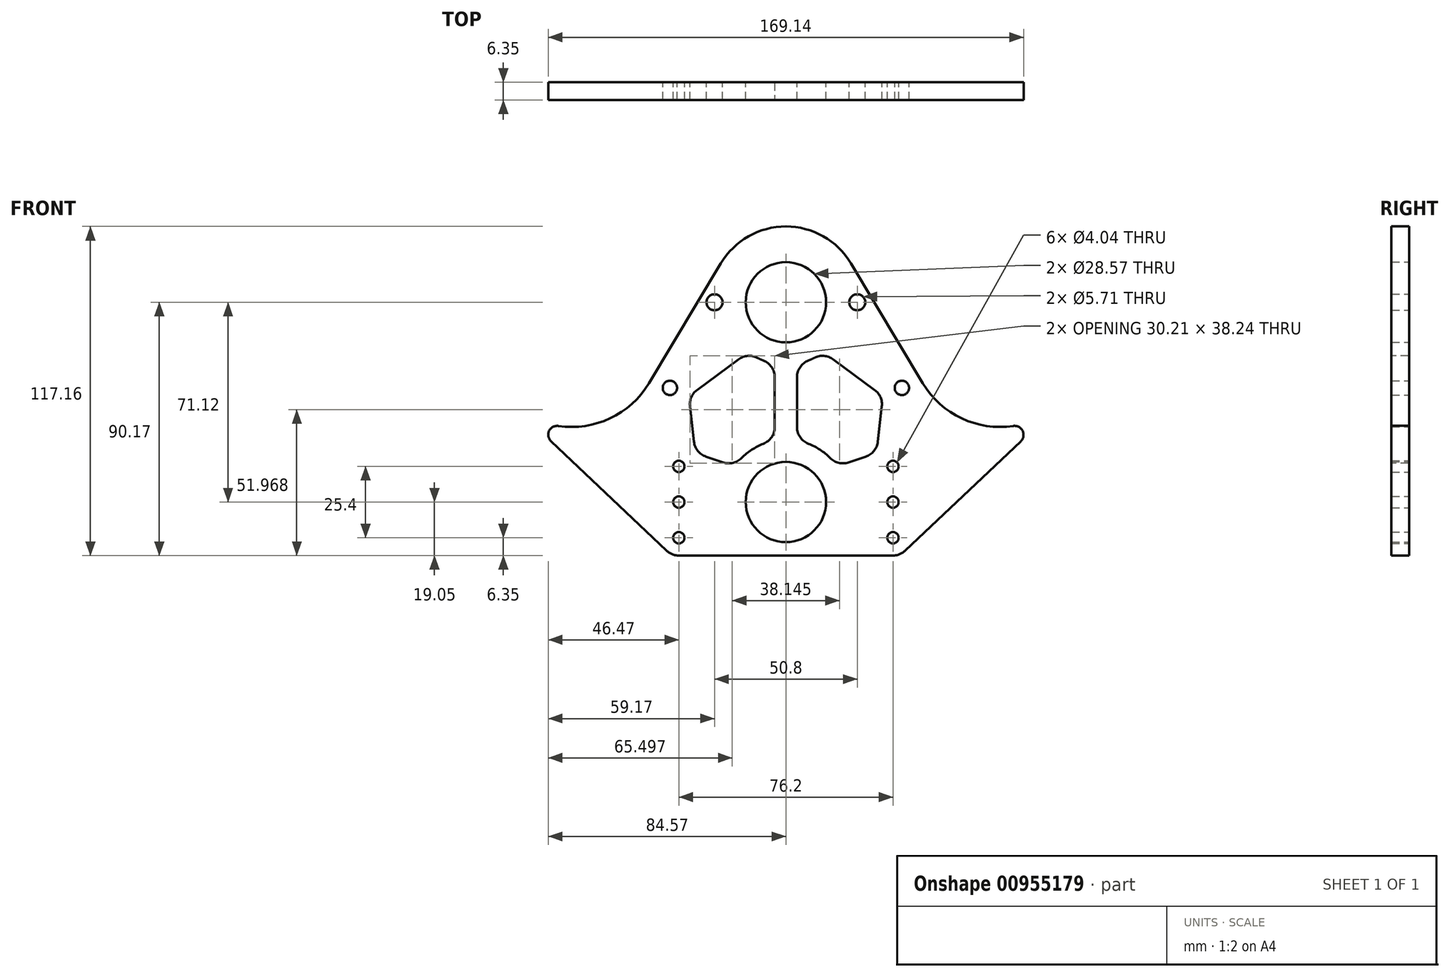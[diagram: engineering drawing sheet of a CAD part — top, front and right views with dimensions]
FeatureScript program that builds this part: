
annotation { "Feature Type Name" : "Feature", "Feature Type Description" : "" }
export const myFeature = defineFeature(function(context is Context, id is Id, definition is map)
    precondition{}
    {
        {
            var Q0;
            Q0=qCreatedBy(makeId("Front.planeOp"),FACE);
            var sketch = newSketch(context, id + "F0", { "sketchPlane" : qUnion([Q0])});
            skCircle(sketch, "E0", {"center": v(-76.2, 58.74) * mm, "radius": 32 * mm, "construction": true});
            skCircle(sketch, "E1", {"center": v(76.2, 58.74) * mm, "radius": 32 * mm, "construction": true});
            skLineSegment(sketch, "E2", {"start": v(-76.2, 58.74) * mm, "end": v(76.2, 58.74) * mm, "construction": true});
            skLineSegment(sketch, "E3", {"start": v(0, 58.74) * mm, "end": v(0, 0) * mm, "construction": true});
            skLineSegment(sketch, "E4.bottom", {"start": v(-127, 23.81) * mm, "end": v(127, 23.81) * mm, "construction": true});
            skLineSegment(sketch, "E4.top", {"start": v(-127, -26.99) * mm, "end": v(127, -26.99) * mm, "construction": true});
            skLineSegment(sketch, "E4.left", {"start": v(-127, 23.81) * mm, "end": v(-127, -26.99) * mm, "construction": true});
            skLineSegment(sketch, "E4.right", {"start": v(127, 23.81) * mm, "end": v(127, -26.99) * mm, "construction": true});
            skPoint(sketch, "E4.middle", {"position": v(0, -1.59) * mm});
            skCircle(sketch, "E5", {"center": v(0, 0) * mm, "radius": 50.8 * mm, "construction": true});
            skCircle(sketch, "E6", {"center": v(0, 71.12) * mm, "radius": 34.3 * mm, "construction": true});
            skCircle(sketch, "E7", {"center": v(0, 71.12) * mm, "radius": 26.99 * mm, "construction": true});
            skCircle(sketch, "E8", {"center": v(0, 71.12) * mm, "radius": 38.1 * mm, "construction": true});
            skCircle(sketch, "E9", {"center": v(0, 0) * mm, "radius": 33.02 * mm, "construction": true});
            skCircle(sketch, "E10", {"center": v(0, 0) * mm, "radius": 44.13 * mm, "construction": true});
            skCircle(sketch, "E11", {"center": v(0, 71.12) * mm, "radius": 14.29 * mm});
            skCircle(sketch, "E12", {"center": v(0, 0) * mm, "radius": 14.29 * mm});
            skCircle(sketch, "E13", {"center": v(-38.1, 12.7) * mm, "radius": 6.35 * mm, "construction": true});
            skCircle(sketch, "E14", {"center": v(-38.1, -12.7) * mm, "radius": 6.35 * mm, "construction": true});
            skCircle(sketch, "E15", {"center": v(38.1, -12.7) * mm, "radius": 6.35 * mm, "construction": true});
            skCircle(sketch, "E16", {"center": v(38.1, 12.7) * mm, "radius": 6.35 * mm, "construction": true});
            skCircle(sketch, "E17", {"center": v(38.1, 0) * mm, "radius": 6.35 * mm, "construction": true});
            skCircle(sketch, "E18", {"center": v(-38.1, 0) * mm, "radius": 6.35 * mm, "construction": true});
            skCircle(sketch, "E19", {"center": v(38.1, -12.7) * mm, "radius": 2.02 * mm});
            skCircle(sketch, "E20", {"center": v(38.1, 0) * mm, "radius": 2.02 * mm});
            skCircle(sketch, "E21", {"center": v(38.1, 12.7) * mm, "radius": 2.02 * mm});
            skCircle(sketch, "E22", {"center": v(-38.1, 12.7) * mm, "radius": 2.02 * mm});
            skCircle(sketch, "E23", {"center": v(-38.1, 0) * mm, "radius": 2.02 * mm});
            skCircle(sketch, "E24", {"center": v(-38.1, -12.7) * mm, "radius": 2.02 * mm});
            skArc(sketch, "E25", {"start": v(-80.92, 27.08) * mm, "mid": v(-62.53, 29.8) * mm, "end": v(-48.75, 42.28) * mm});
            skLineSegment(sketch, "E26", {"start": v(-83.58, 21.64) * mm, "end": v(-42.47, -17.3) * mm});
            skPoint(sketch, "E27.visualSharp", {"position": v(-98.21, 35.5) * mm});
            skArc(sketch, "E27.filletArc", {"start": v(-80.92, 27.08) * mm, "mid": v(-84.25, 25.33) * mm, "end": v(-83.58, 21.64) * mm});
            skLineSegment(sketch, "E28", {"start": v(-48.75, 42.28) * mm, "end": v(-23.15, 85) * mm});
            skArc(sketch, "E29", {"start": v(-23.15, 85) * mm, "mid": v(0, 98.1) * mm, "end": v(23.15, 85) * mm});
            skLineSegment(sketch, "E30", {"start": v(23.15, 85) * mm, "end": v(48.75, 42.28) * mm});
            skArc(sketch, "E31", {"start": v(48.75, 42.28) * mm, "mid": v(62.53, 29.8) * mm, "end": v(80.92, 27.08) * mm});
            skLineSegment(sketch, "E32", {"start": v(83.58, 21.64) * mm, "end": v(42.47, -17.3) * mm});
            skArc(sketch, "E33", {"start": v(-42.47, -17.3) * mm, "mid": v(-40.45, -18.6) * mm, "end": v(-38.1, -19.05) * mm});
            skArc(sketch, "E34", {"start": v(42.47, -17.3) * mm, "mid": v(40.45, -18.6) * mm, "end": v(38.1, -19.05) * mm});
            skLineSegment(sketch, "E35", {"start": v(38.1, -19.05) * mm, "end": v(-38.1, -19.05) * mm});
            skPoint(sketch, "E36.visualSharp", {"position": v(98.21, 35.5) * mm});
            skArc(sketch, "E36.filletArc", {"start": v(83.58, 21.64) * mm, "mid": v(84.25, 25.33) * mm, "end": v(80.92, 27.08) * mm});
            skLineSegment(sketch, "E37.bottom", {"start": v(-38.1, 12.7) * mm, "end": v(38.1, 12.7) * mm, "construction": true});
            skLineSegment(sketch, "E37.top", {"start": v(-38.1, -12.7) * mm, "end": v(38.1, -12.7) * mm, "construction": true});
            skLineSegment(sketch, "E37.left", {"start": v(-38.1, 12.7) * mm, "end": v(-38.1, -12.7) * mm, "construction": true});
            skLineSegment(sketch, "E37.right", {"start": v(38.1, 12.7) * mm, "end": v(38.1, -12.7) * mm, "construction": true});
            skLineSegment(sketch, "E38", {"start": v(-25.4, 71.12) * mm, "end": v(0, 71.12) * mm, "construction": true});
            skLineSegment(sketch, "E39", {"start": v(0, 71.12) * mm, "end": v(25.4, 71.12) * mm, "construction": true});
            skCircle(sketch, "E40", {"center": v(-25.4, 71.12) * mm, "radius": 4.76 * mm, "construction": true});
            skCircle(sketch, "E41", {"center": v(25.4, 71.12) * mm, "radius": 4.76 * mm, "construction": true});
            skCircle(sketch, "E42", {"center": v(-25.4, 71.12) * mm, "radius": 2.86 * mm});
            skCircle(sketch, "E43", {"center": v(25.4, 71.12) * mm, "radius": 2.86 * mm});
            skCircle(sketch, "E44", {"center": v(41.28, 40.64) * mm, "radius": 6.35 * mm, "construction": true});
            skCircle(sketch, "E45", {"center": v(41.28, 40.64) * mm, "radius": 2.55 * mm});
            skCircle(sketch, "E46.MirrorC", {"center": v(-41.28, 40.64) * mm, "radius": 6.35 * mm, "construction": true});
            skCircle(sketch, "E47.MirrorC", {"center": v(-41.28, 40.64) * mm, "radius": 2.55 * mm});
            skSolve(sketch);
        }
        {
            var Q0;
            Q0=qSketchRegion(id+"F0",true);
            extrude(context, id + "F1", {"entities" : qUnion([Q0]), "depth" : 6.35 * mm, "offsetDistance" : 25.4 * mm});
        }
        {
            var Q0;
            Q0=makeQuery(id+"F1.opExtrude","CAP_FACE",FACE,{"disambiguationData":[OSD([sQuery(id+"F0.wireOp",EDGE,"E11"),sQuery(id+"F0.wireOp",EDGE,"E12"),sQuery(id+"F0.wireOp",EDGE,"E19"),sQuery(id+"F0.wireOp",EDGE,"E20"),sQuery(id+"F0.wireOp",EDGE,"E21"),sQuery(id+"F0.wireOp",EDGE,"E22"),sQuery(id+"F0.wireOp",EDGE,"E23"),sQuery(id+"F0.wireOp",EDGE,"E24"),sQuery(id+"F0.wireOp",EDGE,"E25"),sQuery(id+"F0.wireOp",EDGE,"E26"),sQuery(id+"F0.wireOp",EDGE,"E27.filletArc"),sQuery(id+"F0.wireOp",EDGE,"E28"),sQuery(id+"F0.wireOp",EDGE,"E29"),sQuery(id+"F0.wireOp",EDGE,"E30"),sQuery(id+"F0.wireOp",EDGE,"E31"),sQuery(id+"F0.wireOp",EDGE,"E32"),sQuery(id+"F0.wireOp",EDGE,"E33"),sQuery(id+"F0.wireOp",EDGE,"E34"),sQuery(id+"F0.wireOp",EDGE,"E35"),sQuery(id+"F0.wireOp",EDGE,"E36.filletArc"),sQuery(id+"F0.wireOp",EDGE,"E42"),sQuery(id+"F0.wireOp",EDGE,"E43"),sQuery(id+"F0.wireOp",EDGE,"E45"),sQuery(id+"F0.wireOp",EDGE,"E47.MirrorC")])],"isStart":false});
            var sketch = newSketch(context, id + "F2", { "sketchPlane" : qUnion([Q0])});
            skCircle(sketch, "E48", {"center": v(0, 0) * mm, "radius": 22.23 * mm, "construction": true});
            skCircle(sketch, "E49", {"center": v(0, 71.12) * mm, "radius": 22.23 * mm, "construction": true});
            skLineSegment(sketch, "E50", {"start": v(0, 71.12) * mm, "end": v(0, 0) * mm, "construction": true});
            skLineSegment(sketch, "E51", {"start": v(3.97, 21.87) * mm, "end": v(3.97, 49.25) * mm});
            skLineSegment(sketch, "E52", {"start": v(-3.97, 21.87) * mm, "end": v(-3.97, 49.25) * mm});
            skCircle(sketch, "E53", {"center": v(-38.1, 12.7) * mm, "radius": 7.94 * mm, "construction": true});
            skCircle(sketch, "E54", {"center": v(38.1, 12.7) * mm, "radius": 7.94 * mm, "construction": true});
            skCircle(sketch, "E55", {"center": v(41.28, 40.64) * mm, "radius": 7.94 * mm, "construction": true});
            skCircle(sketch, "E56", {"center": v(-41.28, 40.64) * mm, "radius": 7.94 * mm, "construction": true});
            skLineSegment(sketch, "E57", {"start": v(-38.1, 12.7) * mm, "end": v(-41.28, 40.64) * mm, "construction": true});
            skLineSegment(sketch, "E58", {"start": v(-41.28, 40.64) * mm, "end": v(0, 71.12) * mm, "construction": true});
            skLineSegment(sketch, "E59", {"start": v(0, 0) * mm, "end": v(-38.1, 12.7) * mm, "construction": true});
            skLineSegment(sketch, "E60.0", {"start": v(-34.55, 37.71) * mm, "end": v(-13.36, 53.36) * mm});
            skLineSegment(sketch, "E60.1", {"start": v(-32.25, 17.44) * mm, "end": v(-34.55, 37.71) * mm});
            skLineSegment(sketch, "E60.2", {"start": v(-18.2, 12.76) * mm, "end": v(-32.25, 17.44) * mm});
            skArc(sketch, "E61", {"start": v(-3.97, 21.87) * mm, "mid": v(-11.98, 18.72) * mm, "end": v(-18.2, 12.76) * mm});
            skArc(sketch, "E62", {"start": v(-3.97, 49.25) * mm, "mid": v(-8.9, 50.76) * mm, "end": v(-13.36, 53.36) * mm});
            skLineSegment(sketch, "E63.MirrorCS", {"start": v(0, 0) * mm, "end": v(38.1, 12.7) * mm, "construction": true});
            skArc(sketch, "E64.MirrorCS", {"start": v(3.97, 49.25) * mm, "mid": v(8.9, 50.76) * mm, "end": v(13.36, 53.36) * mm});
            skLineSegment(sketch, "E65.MirrorCS", {"start": v(34.55, 37.71) * mm, "end": v(13.36, 53.36) * mm});
            skLineSegment(sketch, "E66.MirrorCS", {"start": v(38.1, 12.7) * mm, "end": v(41.28, 40.64) * mm, "construction": true});
            skLineSegment(sketch, "E67.MirrorCS", {"start": v(18.2, 12.76) * mm, "end": v(32.25, 17.44) * mm});
            skArc(sketch, "E68.MirrorCS", {"start": v(3.97, 21.87) * mm, "mid": v(11.98, 18.72) * mm, "end": v(18.2, 12.76) * mm});
            skLineSegment(sketch, "E69.MirrorCS", {"start": v(41.28, 40.64) * mm, "end": v(0, 71.12) * mm, "construction": true});
            skLineSegment(sketch, "E70.MirrorCS", {"start": v(32.25, 17.44) * mm, "end": v(34.55, 37.71) * mm});
            skSolve(sketch);
        }
        {
            var Q0;
            Q0=qSketchRegion(id+"F2",true);
            extrude(context, id + "F3", {"entities" : qUnion([Q0]), "operationType" : NewBodyOperationType.REMOVE, "endBound" : BoundingType.THROUGH_ALL, "oppositeDirection" : true, "depth" : 25.4 * mm, "offsetDistance" : 25.4 * mm});
        }
        {
            var Q0;
            Q0=makeQuery(id+"F3.boolean.opBoolean","COPY",EDGE,{"derivedFrom":makeQuery(id+"F3.opExtrude","SWEPT_EDGE",EDGE,{"disambiguationData":[OSD([sQuery(id+"F2.wireOp",EDGE,"E60.0"),sQuery(id+"F2.wireOp",EDGE,"E62")])]})});
            var Q1;
            Q1=makeQuery(id+"F3.boolean.opBoolean","COPY",EDGE,{"derivedFrom":makeQuery(id+"F3.opExtrude","SWEPT_EDGE",EDGE,{"disambiguationData":[OSD([sQuery(id+"F2.wireOp",EDGE,"E62"),sQuery(id+"F2.wireOp",EDGE,"E52")])]})});
            var Q2;
            Q2=makeQuery(id+"F3.boolean.opBoolean","COPY",EDGE,{"derivedFrom":makeQuery(id+"F3.opExtrude","SWEPT_EDGE",EDGE,{"disambiguationData":[OSD([sQuery(id+"F2.wireOp",EDGE,"E61"),sQuery(id+"F2.wireOp",EDGE,"E52")])]})});
            var Q3;
            Q3=makeQuery(id+"F3.boolean.opBoolean","COPY",EDGE,{"derivedFrom":makeQuery(id+"F3.opExtrude","SWEPT_EDGE",EDGE,{"disambiguationData":[OSD([sQuery(id+"F2.wireOp",EDGE,"E60.2"),sQuery(id+"F2.wireOp",EDGE,"E61")])]})});
            var Q4;
            Q4=makeQuery(id+"F3.boolean.opBoolean","COPY",EDGE,{"derivedFrom":makeQuery(id+"F3.opExtrude","SWEPT_EDGE",EDGE,{"disambiguationData":[OSD([sQuery(id+"F2.wireOp",EDGE,"E60.1"),sQuery(id+"F2.wireOp",EDGE,"E60.2")])]})});
            var Q5;
            Q5=makeQuery(id+"F3.boolean.opBoolean","COPY",EDGE,{"derivedFrom":makeQuery(id+"F3.opExtrude","SWEPT_EDGE",EDGE,{"disambiguationData":[OSD([sQuery(id+"F2.wireOp",EDGE,"E60.0"),sQuery(id+"F2.wireOp",EDGE,"E60.1")])]})});
            var Q6;
            Q6=makeQuery(id+"F3.boolean.opBoolean","COPY",EDGE,{"derivedFrom":makeQuery(id+"F3.opExtrude","SWEPT_EDGE",EDGE,{"disambiguationData":[OSD([sQuery(id+"F2.wireOp",EDGE,"E64.MirrorCS"),sQuery(id+"F2.wireOp",EDGE,"E51")])]})});
            var Q7;
            Q7=makeQuery(id+"F3.boolean.opBoolean","COPY",EDGE,{"derivedFrom":makeQuery(id+"F3.opExtrude","SWEPT_EDGE",EDGE,{"disambiguationData":[OSD([sQuery(id+"F2.wireOp",EDGE,"E64.MirrorCS"),sQuery(id+"F2.wireOp",EDGE,"E65.MirrorCS")])]})});
            var Q8;
            Q8=makeQuery(id+"F3.boolean.opBoolean","COPY",EDGE,{"derivedFrom":makeQuery(id+"F3.opExtrude","SWEPT_EDGE",EDGE,{"disambiguationData":[OSD([sQuery(id+"F2.wireOp",EDGE,"E65.MirrorCS"),sQuery(id+"F2.wireOp",EDGE,"E70.MirrorCS")])]})});
            var Q9;
            Q9=makeQuery(id+"F3.boolean.opBoolean","COPY",EDGE,{"derivedFrom":makeQuery(id+"F3.opExtrude","SWEPT_EDGE",EDGE,{"disambiguationData":[OSD([sQuery(id+"F2.wireOp",EDGE,"E67.MirrorCS"),sQuery(id+"F2.wireOp",EDGE,"E70.MirrorCS")])]})});
            var Q10;
            Q10=makeQuery(id+"F3.boolean.opBoolean","COPY",EDGE,{"derivedFrom":makeQuery(id+"F3.opExtrude","SWEPT_EDGE",EDGE,{"disambiguationData":[OSD([sQuery(id+"F2.wireOp",EDGE,"E67.MirrorCS"),sQuery(id+"F2.wireOp",EDGE,"E68.MirrorCS")])]})});
            var Q11;
            Q11=makeQuery(id+"F3.boolean.opBoolean","COPY",EDGE,{"derivedFrom":makeQuery(id+"F3.opExtrude","SWEPT_EDGE",EDGE,{"disambiguationData":[OSD([sQuery(id+"F2.wireOp",EDGE,"E68.MirrorCS"),sQuery(id+"F2.wireOp",EDGE,"E51")])]})});
            fillet(context, id + "F4", {"entities" : qUnion([Q0, Q1, Q2, Q3, Q4, Q5, Q6, Q7, Q8, Q9, Q10, Q11]), "radius" : 6.35 * mm, "tangentPropagation" : true, "allowEdgeOverflow" : false});
        }
    });
